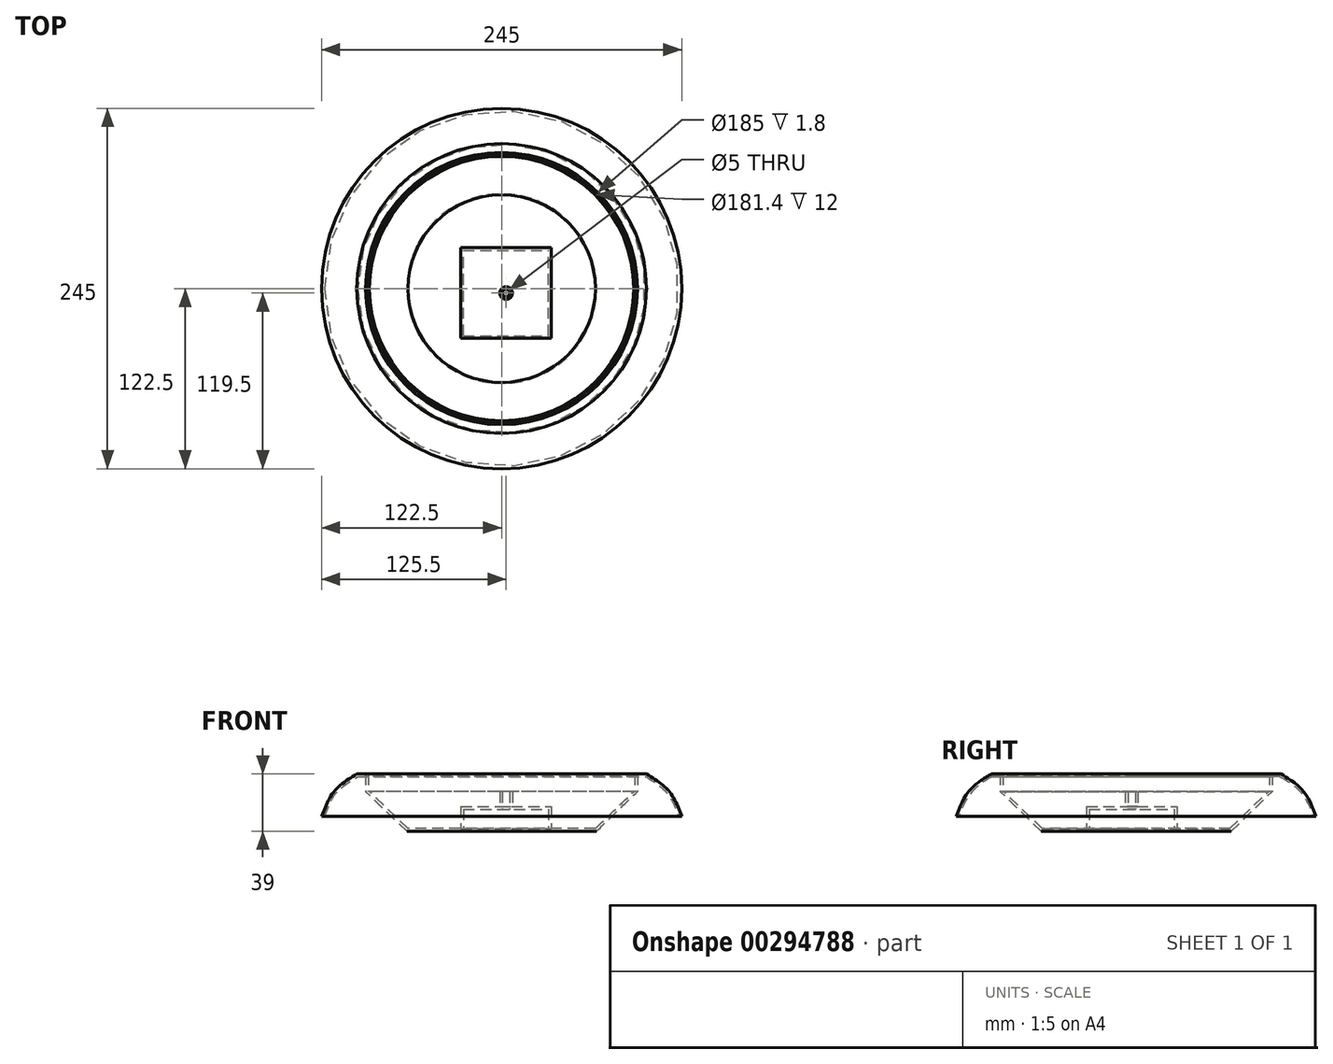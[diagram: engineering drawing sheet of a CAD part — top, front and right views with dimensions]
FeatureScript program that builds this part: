
annotation { "Feature Type Name" : "Feature", "Feature Type Description" : "" }
export const myFeature = defineFeature(function(context is Context, id is Id, definition is map)
    precondition{}
    {
        {
            var Q0;
            Q0=qCreatedBy(makeId("Top.planeOp"),FACE);
            var sketch = newSketch(context, id + "F0", { "sketchPlane" : qUnion([Q0])});
            skCircle(sketch, "E0", {"center": v(0, 0) * mm, "radius": 98.5 * mm});
            skSolve(sketch);
        }
        {
            var Q0;
            Q0=qCreatedBy(makeId("Top.planeOp"),FACE);
            cPlane(context, id + "F1", {"entities" : qUnion([Q0]), "cplaneType" : CPlaneType.OFFSET, "offset" : 29 * mm, "oppositeDirection" : true, "width" : 150 * mm, "height" : 150 * mm});
        }
        {
            var Q0;
            Q0=qCreatedBy(id+"F1.planeOp",FACE);
            var sketch = newSketch(context, id + "F2", { "sketchPlane" : qUnion([Q0])});
            skCircle(sketch, "E1", {"center": v(0, 0) * mm, "radius": 122.5 * mm});
            skSolve(sketch);
        }
        {
            var Q0;
            Q0=qCreatedBy(id+"F1.planeOp",FACE);
            cPlane(context, id + "F3", {"entities" : qUnion([Q0]), "cplaneType" : CPlaneType.OFFSET, "offset" : 17 * mm, "width" : 150 * mm, "height" : 150 * mm});
        }
        {
            var Q0;
            Q0=qCreatedBy(id+"F3.planeOp",FACE);
            var sketch = newSketch(context, id + "F4", { "sketchPlane" : qUnion([Q0])});
            skCircle(sketch, "E2", {"center": v(0, 0) * mm, "radius": 114 * mm});
            skSolve(sketch);
        }
        {
            var Q0;
            Q0=makeQuery(id+"F2.imprint","IMPRINT",FACE,{"disambiguationData":[TD([[makeQuery(id+"F2.imprint","IMPRINT",EDGE,{"derivedFrom":sQuery(id+"F2.wireOp",EDGE,"E1")}),1.0]])]});
            var Q1;
            Q1=makeQuery(id+"F4.imprint","IMPRINT",FACE,{"disambiguationData":[TD([[makeQuery(id+"F4.imprint","IMPRINT",EDGE,{"derivedFrom":sQuery(id+"F4.wireOp",EDGE,"E2")}),1.0]])]});
            var Q2;
            Q2=makeQuery(id+"F0.imprint","IMPRINT",FACE,{"disambiguationData":[TD([[makeQuery(id+"F0.imprint","IMPRINT",EDGE,{"derivedFrom":sQuery(id+"F0.wireOp",EDGE,"E0")}),1.0]])]});
            var Q3;
            Q3=sQuery(id+"F2.wireOp",EDGE,"E1");
            var Q4;
            Q4=sQuery(id+"F4.wireOp",EDGE,"E2");
            var Q5;
            Q5=sQuery(id+"F0.wireOp",EDGE,"E0");
            loft(context, id + "F5", {"sheetProfilesArray" : [{ "sheetProfileEntities" : qUnion([Q0]) }, { "sheetProfileEntities" : qUnion([Q1]) }, { "sheetProfileEntities" : qUnion([Q2]) }], "wireProfilesArray" : [{ "wireProfileEntities" : qUnion([Q3]) }, { "wireProfileEntities" : qUnion([Q4]) }, { "wireProfileEntities" : qUnion([Q5]) }]});
        }
        {
            var Q0;
            Q0=makeQuery(id+"F5.opLoft","CAP_FACE",FACE,{"disambiguationData":[OSD([makeQuery(id+"F0.imprint","IMPRINT",FACE,{"disambiguationData":[TD([[makeQuery(id+"F0.imprint","IMPRINT",EDGE,{"derivedFrom":sQuery(id+"F0.wireOp",EDGE,"E0")}),1.0]])]})])],"isStart":true});
            var sketch = newSketch(context, id + "F6", { "sketchPlane" : qUnion([Q0])});
            skCircle(sketch, "E3", {"center": v(0, 0) * mm, "radius": 92.5 * mm});
            skSolve(sketch);
        }
        {
            var Q0;
            Q0 = qSketchRegion(id + "F6", true);
            extrude(context, id + "F7", {"entities" : qUnion([Q0]), "operationType" : NewBodyOperationType.REMOVE, "oppositeDirection" : true, "depth" : 1.8 * mm});
        }
        {
            var Q0;
            Q0=makeQuery(id+"F7.boolean.opBoolean","COPY",FACE,{"derivedFrom":makeQuery(id+"F7.opExtrude","CAP_FACE",FACE,{"disambiguationData":[OSD([sQuery(id+"F6.wireOp",EDGE,"E3")])],"isStart":false})});
            var Q1;
            Q1=makeQuery(id+"F5.opLoft","CAP_FACE",FACE,{"disambiguationData":[OSD([makeQuery(id+"F2.imprint","IMPRINT",FACE,{"disambiguationData":[TD([[makeQuery(id+"F2.imprint","IMPRINT",EDGE,{"derivedFrom":sQuery(id+"F2.wireOp",EDGE,"E1")}),1.0]])]})])],"isStart":true});
            var Q2;
            Q2=makeQuery(id+"F7.boolean.opBoolean","COPY",FACE,{"derivedFrom":makeQuery(id+"F7.opExtrude","SWEPT_FACE",FACE,{"disambiguationData":[OSD([sQuery(id+"F6.wireOp",EDGE,"E3")])]})});
            shell(context, id + "F8", {"entities" : qUnion([Q0, Q1, Q2]), "thickness" : 1.8 * mm});
        }
        {
            var Q0;
            Q0=qCreatedBy(makeId("Top.planeOp"),FACE);
            cPlane(context, id + "F9", {"entities" : qUnion([Q0]), "cplaneType" : CPlaneType.OFFSET, "offset" : 39 * mm, "oppositeDirection" : true, "width" : 150 * mm, "height" : 150 * mm});
        }
        {
            var Q0;
            Q0=qCreatedBy(id+"F9.planeOp",FACE);
            var sketch = newSketch(context, id + "F10", { "sketchPlane" : qUnion([Q0])});
            skCircle(sketch, "E4", {"center": v(0, 0) * mm, "radius": 64.5 * mm});
            skSolve(sketch);
        }
        {
            var Q0;
            Q0=qCreatedBy(id+"F1.planeOp",FACE);
            cPlane(context, id + "F11", {"entities" : qUnion([Q0]), "cplaneType" : CPlaneType.OFFSET, "offset" : 17 * mm, "width" : 150 * mm, "height" : 150 * mm});
        }
        {
            var Q0;
            Q0=qCreatedBy(id+"F11.planeOp",FACE);
            var sketch = newSketch(context, id + "F12", { "sketchPlane" : qUnion([Q0])});
            skCircle(sketch, "E5", {"center": v(0, 0) * mm, "radius": 92.5 * mm});
            skSolve(sketch);
        }
        {
            var Q0;
            Q0=makeQuery(id+"F10.imprint","IMPRINT",FACE,{"disambiguationData":[TD([[makeQuery(id+"F10.imprint","IMPRINT",EDGE,{"derivedFrom":sQuery(id+"F10.wireOp",EDGE,"E4")}),1.0]])]});
            var Q1;
            Q1 = qSketchRegion(id + "F12", true);
            loft(context, id + "F13", {"sheetProfilesArray" : [{ "sheetProfileEntities" : qUnion([Q0]) }, { "sheetProfileEntities" : qUnion([Q1]) }]});
        }
        {
            var Q0;
            Q0=makeQuery(id+"F13.opLoft","CAP_FACE",FACE,{"disambiguationData":[OSD([makeQuery(id+"F10.imprint","IMPRINT",FACE,{"disambiguationData":[TD([[makeQuery(id+"F10.imprint","IMPRINT",EDGE,{"derivedFrom":sQuery(id+"F10.wireOp",EDGE,"E4")}),1.0]])]})])],"isStart":true});
            var sketch = newSketch(context, id + "F14", { "sketchPlane" : qUnion([Q0])});
            skLineSegment(sketch, "E6.bottom", {"start": v(-26, 32) * mm, "end": v(32, 32) * mm});
            skLineSegment(sketch, "E6.top", {"start": v(-26, -26) * mm, "end": v(32, -26) * mm});
            skLineSegment(sketch, "E6.left", {"start": v(-26, 32) * mm, "end": v(-26, -26) * mm});
            skLineSegment(sketch, "E6.right", {"start": v(32, 32) * mm, "end": v(32, -26) * mm});
            skSolve(sketch);
        }
        {
            var Q0;
            Q0 = qSketchRegion(id + "F14", true);
            extrude(context, id + "F15", {"entities" : qUnion([Q0]), "operationType" : NewBodyOperationType.REMOVE, "oppositeDirection" : true, "depth" : 15 * mm});
        }
        {
            var Q0;
            Q0=makeQuery(id+"F15.boolean.opBoolean","COPY",FACE,{"derivedFrom":makeQuery(id+"F15.opExtrude","CAP_FACE",FACE,{"disambiguationData":[OSD([sQuery(id+"F14.wireOp",EDGE,"E6.bottom"),sQuery(id+"F14.wireOp",EDGE,"E6.top"),sQuery(id+"F14.wireOp",EDGE,"E6.left"),sQuery(id+"F14.wireOp",EDGE,"E6.right")])],"isStart":false})});
            var sketch = newSketch(context, id + "F16", { "sketchPlane" : qUnion([Q0])});
            skCircle(sketch, "E7", {"center": v(3, 3) * mm, "radius": 2.5 * mm});
            skSolve(sketch);
        }
        {
            var Q0;
            Q0 = qSketchRegion(id + "F16", true);
            extrude(context, id + "F17", {"entities" : qUnion([Q0]), "operationType" : NewBodyOperationType.REMOVE, "endBound" : BoundingType.THROUGH_ALL, "oppositeDirection" : true, "depth" : 25 * mm});
        }
        {
            var Q0;
            Q0=makeQuery(id+"F13.opLoft","CAP_FACE",FACE,{"disambiguationData":[OSD([makeQuery(id+"F12.imprint","IMPRINT",FACE,{"disambiguationData":[TD([[makeQuery(id+"F12.imprint","IMPRINT",EDGE,{"derivedFrom":sQuery(id+"F12.wireOp",EDGE,"E5")}),1.0]])]})])],"isStart":true});
            shell(context, id + "F18", {"entities" : qUnion([Q0]), "thickness" : 1.8 * mm});
        }
        {
            var Q0;
            Q0=makeQuery(id+"F12.imprint","IMPRINT",FACE,{"disambiguationData":[TD([[makeQuery(id+"F12.imprint","IMPRINT",EDGE,{"derivedFrom":sQuery(id+"F12.wireOp",EDGE,"E5")}),1.0]])]});
            extrude(context, id + "F19", {"entities" : qUnion([Q0]), "depth" : 12 * mm});
        }
        {
            var Q0;
            Q0=makeQuery(id+"F19.opExtrude","CAP_FACE",FACE,{"disambiguationData":[OSD([sQuery(id+"F12.wireOp",EDGE,"E5")])],"isStart":false});
            var Q1;
            Q1=makeQuery(id+"F19.opExtrude","CAP_FACE",FACE,{"disambiguationData":[OSD([sQuery(id+"F12.wireOp",EDGE,"E5")])],"isStart":true});
            shell(context, id + "F20", {"entities" : qUnion([Q0, Q1]), "thickness" : 1.8 * mm});
        }
    });
